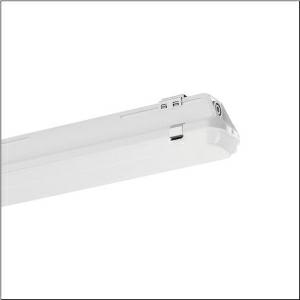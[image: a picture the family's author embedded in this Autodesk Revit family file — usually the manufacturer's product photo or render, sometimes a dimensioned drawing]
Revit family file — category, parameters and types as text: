
# Revit family: monsun_r__21_51fb10dp480c_f104
name_source: partatom
category: Lighting Fixtures
units: mm (PartAtom-declared; Revit-internal decimal feet)

## family parameters
Cut with Voids When Loaded = No
Host = Face
Light Source = No
Part Type = Normal
Room Calculation Point = No
Round Connector Dimension = Use Diameter
Shared = No

## types (1)
- --- (1 x LED, 8090 lm, 46.1 W, 4000K)
    Apparent Load = 46 VA
    CIE Flux Codes = 47 77 93 94 100
    Color Rendering = 80
    Color Temperature = 4000K
    Default Elevation = 1800 mm
    Description = Monsun® 21, damp-proof luminaire, chain hanger, primary optical cover: enclosure, of PMMA, light emission: direct distribution, primary light characteristic: symmetric, installation type: suspended mounting, surface-mounted, horizontal mounting, vertical mounting, LED, rated luminous flux: 8.090lm, luminous efficacy: 176lm/W, light colour: 840, colour temperature: 4000K, control gear: DALI 2, with terminal, 5-pole, max. 2.5mm², mains connection: 220..240V, AC, 50/60Hz, rated input power: 46W, housing, of glass-fibre reinforced polyester, uncoated, bright grey, incl. chain hanger, length: 1.590mm, width: 90mm, height: 88mm, clip for enclosure, of stainless steel (V2A), ceiling mounting element, of stainless steel (V2A), chain hanger, of stainless steel (V2A), protection rating (complete): IP66, insulation class (complete): insulation class I (protective earthing), certification: CE, ENEC, VDE, UKCA, protection symbol: D, impact resistance: IK04, permissible operating ambient temperature: -25..+35°C, standard: EN 50419, EN 60598-2-1, corresponds to IFS (International Featured Standards) requirements for safety and quality in the food industry, for indoor or canopied outdoor use, no direct snow, no direct sun, no direct rain, LABS conformity tested according to VDMA 24364:2018-05, contact your sales advisor before using the luminaires in applications with unclear chemical exposure, large temperature fluctuations or condensation-forming humidity, packaging unit: 1 piece
    Height = 89 mm
    Lamp = 1 x LED
    Lamp Light Flux = 8090 lm
    Lamp Power = 46.1 W
    Lamp count = 1
    Length = 1590 mm
    Luminous efficacy = 175 lm/W
    Manufacturer = Siteco
    ModVariant = No
    Model = 51FB10DP480C
    Mounting Place = Ceiling
    Mounting Type = Surface mounted
    Number of Poles = 1
    OnlyDefault = Yes
    Power Factor = 1
    Product Name = Monsun® 21
    Product group = damp-proof luminaire
    ProductGroupID = 301
    Protection Class = Protection class I
    Protection Degree = IP 66
    RLX_Detail_Level = 1
    RLX_Emergency_Light_Flux = 0 lm
    RLX_Emergency_Type = 0
    RLX_Emergency_Type_DB = No
    RlxData = <blob elided: 92021 chars, md5=84fd5f0a>
    Socket = socket
    Standby Power = 0 W
    System Light Flux = 8090 lm
    System Power = 46 W
    Type Comments = factory setting: luminous flux: 100 % | dim-lin: 254 | 311 mA
    Type Image = l_1319656.jpg
    URL = http://relux.com
    VarID = @adj_051881
    Voltage = 0 V
    Weight = 0.00 kg
    Width = 90 mm

## geometry (parser evidence)
native form markers: Blend x4, Sweep x13
no freeform markers — native parametric forms only
